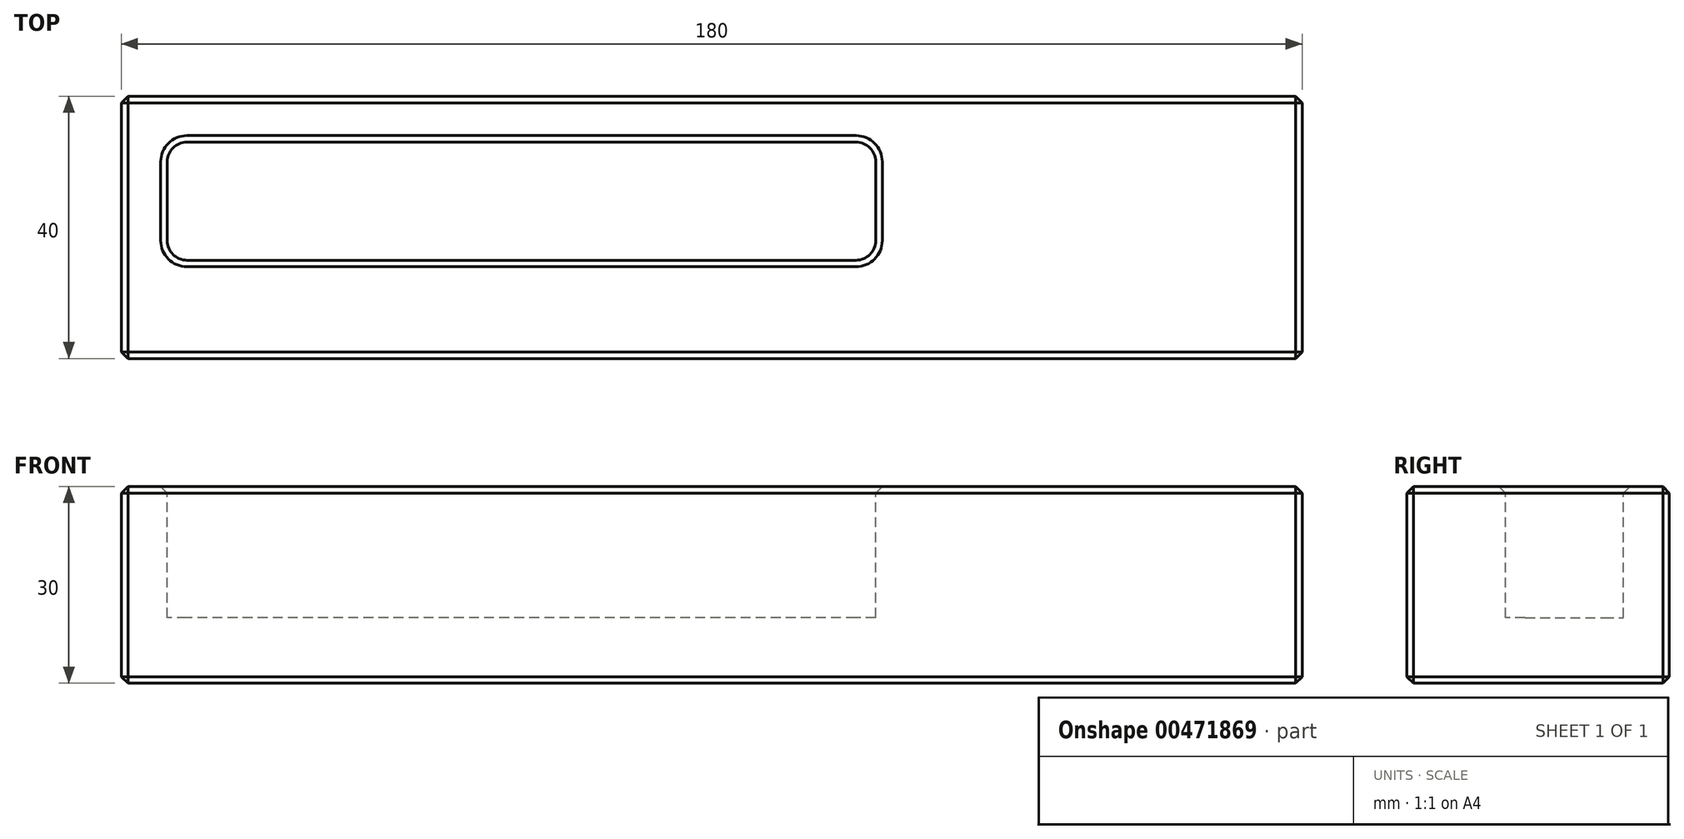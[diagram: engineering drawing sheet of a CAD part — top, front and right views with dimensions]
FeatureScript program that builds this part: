
annotation { "Feature Type Name" : "Feature", "Feature Type Description" : "" }
export const myFeature = defineFeature(function(context is Context, id is Id, definition is map)
    precondition{}
    {
        {
            var Q0;
            Q0=qCreatedBy(makeId("Right.planeOp"),FACE);
            var sketch = newSketch(context, id + "F0", { "sketchPlane" : qUnion([Q0])});
            skLineSegment(sketch, "E0.bottom", {"start": v(-20, 15) * mm, "end": v(20, 15) * mm});
            skLineSegment(sketch, "E0.top", {"start": v(-20, -15) * mm, "end": v(20, -15) * mm});
            skLineSegment(sketch, "E0.left", {"start": v(-20, 15) * mm, "end": v(-20, -15) * mm});
            skLineSegment(sketch, "E0.right", {"start": v(20, 15) * mm, "end": v(20, -15) * mm});
            skPoint(sketch, "E0.middle", {"position": v(0, 0) * mm});
            skSolve(sketch);
        }
        {
            var Q0;
            Q0=makeQuery(id+"F0.imprint","IMPRINT",FACE,{"disambiguationData":[TD([[makeQuery(id+"F0.imprint","IMPRINT",EDGE,{"derivedFrom":sQuery(id+"F0.wireOp",EDGE,"E0.bottom")}),-1.0]])]});
            extrude(context, id + "F1", {"entities" : qUnion([Q0]), "depth" : 180 * mm});
        }
        {
            var Q0;
            Q0=makeQuery(id+"F1.opExtrude","SWEPT_FACE",FACE,{"disambiguationData":[OSD([sQuery(id+"F0.wireOp",EDGE,"E0.bottom")])]});
            var sketch = newSketch(context, id + "F2", { "sketchPlane" : qUnion([Q0])});
            skLineSegment(sketch, "E1.bottom", {"start": v(112, -5) * mm, "end": v(10, -5) * mm});
            skLineSegment(sketch, "E1.top", {"start": v(112, 13) * mm, "end": v(10, 13) * mm});
            skLineSegment(sketch, "E1.left", {"start": v(115, -2) * mm, "end": v(115, 10) * mm});
            skLineSegment(sketch, "E1.right", {"start": v(7, -2) * mm, "end": v(7, 10) * mm});
            skPoint(sketch, "E1.middle", {"position": v(61, 4) * mm});
            skPoint(sketch, "E2.visualSharp", {"position": v(7, 13) * mm});
            skArc(sketch, "E2.filletArc", {"start": v(10, 13) * mm, "mid": v(7.88, 12.12) * mm, "end": v(7, 10) * mm});
            skPoint(sketch, "E3.visualSharp", {"position": v(115, 13) * mm});
            skArc(sketch, "E3.filletArc", {"start": v(115, 10) * mm, "mid": v(114.12, 12.12) * mm, "end": v(112, 13) * mm});
            skPoint(sketch, "E4.visualSharp", {"position": v(115, -5) * mm});
            skArc(sketch, "E4.filletArc", {"start": v(112, -5) * mm, "mid": v(114.12, -4.12) * mm, "end": v(115, -2) * mm});
            skPoint(sketch, "E5.visualSharp", {"position": v(7, -5) * mm});
            skArc(sketch, "E5.filletArc", {"start": v(7, -2) * mm, "mid": v(7.88, -4.12) * mm, "end": v(10, -5) * mm});
            skSolve(sketch);
        }
        {
            var Q0;
            Q0=makeQuery(id+"F2.imprint","IMPRINT",FACE,{"disambiguationData":[TD([[makeQuery(id+"F2.imprint","IMPRINT",EDGE,{"derivedFrom":sQuery(id+"F2.wireOp",EDGE,"E1.bottom")}),-1.0]])]});
            extrude(context, id + "F3", {"entities" : qUnion([Q0]), "operationType" : NewBodyOperationType.REMOVE, "oppositeDirection" : true, "depth" : 20 * mm});
        }
        {
            var Q0;
            Q0=makeQuery(id+"F1.opExtrude","SWEPT_FACE",FACE,{"disambiguationData":[OSD([sQuery(id+"F0.wireOp",EDGE,"E0.right")])]});
            var Q1;
            Q1=makeQuery(id+"F1.opExtrude","CAP_EDGE",EDGE,{"disambiguationData":[OSD([sQuery(id+"F0.wireOp",EDGE,"E0.bottom")])],"isStart":true});
            var Q2;
            Q2=makeQuery(id+"F1.opExtrude","CAP_EDGE",EDGE,{"disambiguationData":[OSD([sQuery(id+"F0.wireOp",EDGE,"E0.left")])],"isStart":true});
            var Q3;
            Q3=makeQuery(id+"F1.opExtrude","CAP_EDGE",EDGE,{"disambiguationData":[OSD([sQuery(id+"F0.wireOp",EDGE,"E0.top")])],"isStart":true});
            var Q4;
            Q4=makeQuery(id+"F1.opExtrude","SWEPT_EDGE",EDGE,{"disambiguationData":[OSD([sQuery(id+"F0.wireOp",EDGE,"E0.bottom"),sQuery(id+"F0.wireOp",EDGE,"E0.left")])]});
            var Q5;
            Q5=makeQuery(id+"F1.opExtrude","CAP_EDGE",EDGE,{"disambiguationData":[OSD([sQuery(id+"F0.wireOp",EDGE,"E0.bottom")])],"isStart":false});
            var Q6;
            Q6=makeQuery(id+"F3.boolean.opBoolean","COPY",EDGE,{"derivedFrom":makeQuery(id+"F3.opExtrude","CAP_EDGE",EDGE,{"disambiguationData":[OSD([sQuery(id+"F2.wireOp",EDGE,"E1.top")])],"isStart":true})});
            var Q7;
            Q7=makeQuery(id+"F3.boolean.opBoolean","COPY",EDGE,{"derivedFrom":makeQuery(id+"F3.opExtrude","CAP_EDGE",EDGE,{"disambiguationData":[OSD([sQuery(id+"F2.wireOp",EDGE,"E1.left")])],"isStart":true})});
            var Q8;
            Q8=makeQuery(id+"F1.opExtrude","CAP_EDGE",EDGE,{"disambiguationData":[OSD([sQuery(id+"F0.wireOp",EDGE,"E0.left")])],"isStart":false});
            var Q9;
            Q9=makeQuery(id+"F1.opExtrude","SWEPT_EDGE",EDGE,{"disambiguationData":[OSD([sQuery(id+"F0.wireOp",EDGE,"E0.top"),sQuery(id+"F0.wireOp",EDGE,"E0.left")])]});
            var Q10;
            Q10=makeQuery(id+"F1.opExtrude","SWEPT_FACE",FACE,{"disambiguationData":[OSD([sQuery(id+"F0.wireOp",EDGE,"E0.bottom")])]});
            var Q11;
            Q11=makeQuery(id+"F1.opExtrude","CAP_EDGE",EDGE,{"disambiguationData":[OSD([sQuery(id+"F0.wireOp",EDGE,"E0.top")])],"isStart":false});
            chamfer(context, id + "F4", {"entities" : qUnion([Q0, Q1, Q2, Q3, Q4, Q5, Q6, Q7, Q8, Q9, Q10, Q11]), "width" : 1 * mm, "tangentPropagation" : true});
        }
    });
